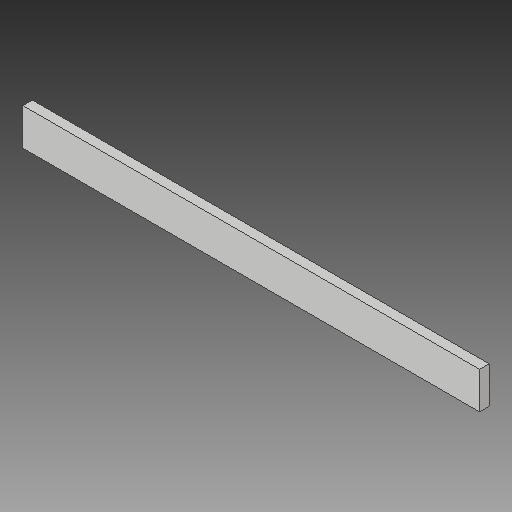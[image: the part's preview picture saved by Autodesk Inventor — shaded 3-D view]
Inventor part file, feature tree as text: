
AUTODESK INVENTOR PART (.ipt)
format: ipt  version: 2019 (Build 230136000, 136)  size: 92,672 bytes
history: native  units: mm
features: extrude x1, sketch x1
ambient origin geometry x8: Origin, YZ Plane, XZ Plane, XY Plane, X Axis, Y Axis, Z Axis, Center Point
bodies: Solid1 (feature_tree)
feature tree (2):
  extrude  "Extrusion1"  Depth=12.0mm
  sketch  "Sketch1"  dims[d0=148.627mm d1=12.0mm d2=3.1mm d3=0.0mm]
